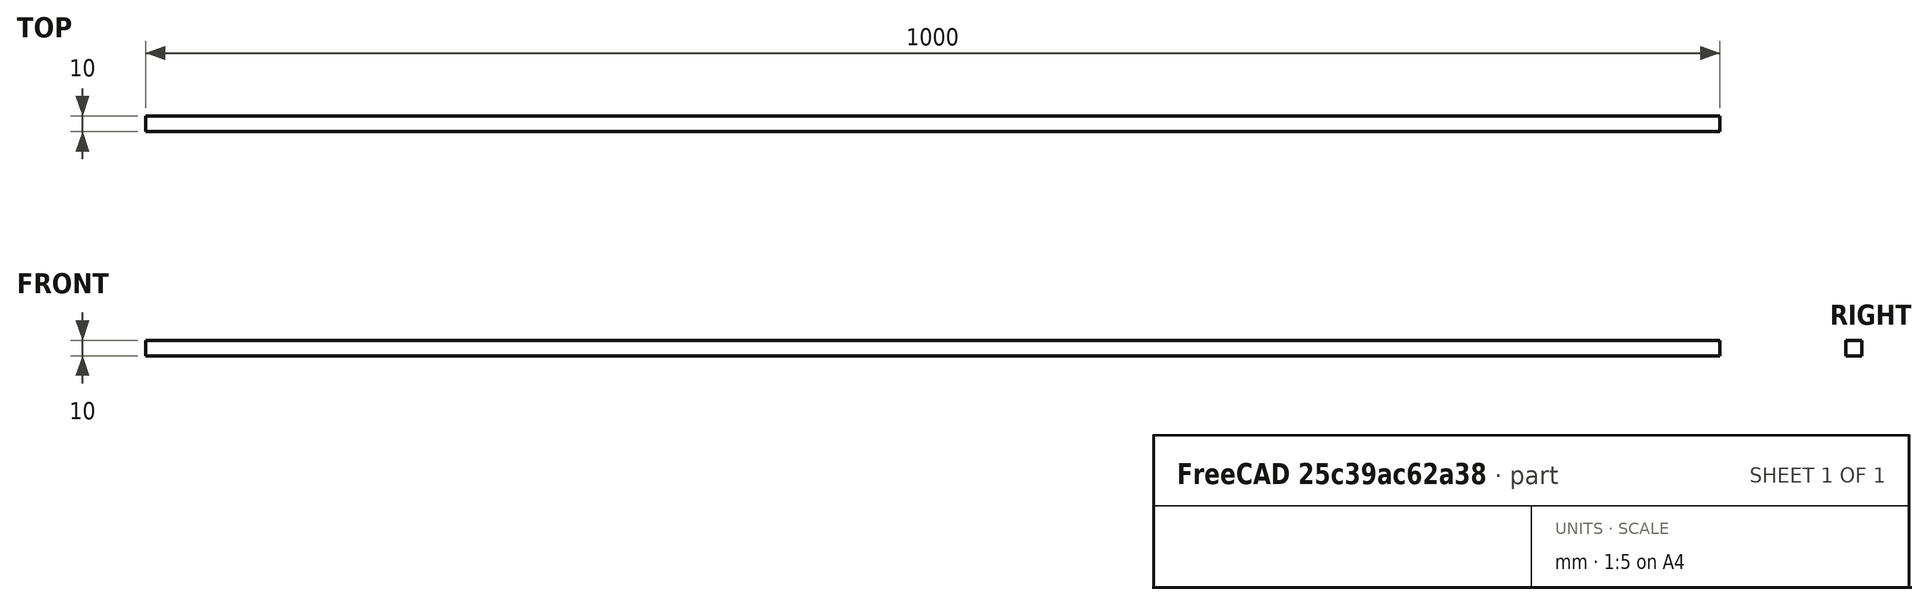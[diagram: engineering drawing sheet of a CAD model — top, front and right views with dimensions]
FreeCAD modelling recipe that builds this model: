
FCSTD DOCUMENT  (FreeCAD 0.21R33694 (Git))
Label: Bar buckling
License: All rights reserved
LicenseURL: http://en.wikipedia.org/wiki/All_rights_reserved
objects: Fem::FemMeshObjectPython×5, Fem::FemResultObjectPython×4, Part::Box×1, Fem::ConstraintFixed×1, Fem::ConstraintForce×1, App::MaterialObjectPython×1, Fem::FemSolverObjectPython×1, Fem::FemAnalysis×1
note: 1 computed .brp shape members not serialized (recipe doc carries the construction recipe); baked Part::Feature solids carry a one-line shape summary decoded from their .brp

FEATURE [Part::Box] Box  label="Cube"
  AttacherType = Attacher::AttachEngine3D
  Height = 10
  Length = 1000
  Width = 10
FEATURE [Fem::ConstraintFixed] ConstraintFixed
  NormalDirection = (-1,0,0)
  Normals = (9) [(-1,0,0),(-1,0,0),(-1,0,0),(-1,0,0),(-1,0,0),(-1,0,0),(-1,0,0),(-1,0,0),(-1,0,0)]
  Points = (9) [(0,10,0),(0,10,5),(0,10,10),(0,5,0),(0,5,5),(0,5,10),(0,0,0),(0,0,5),(0,0,10)]
  References = -> [Box]
FEATURE [Fem::ConstraintForce] ConstraintForce
  DirectionVector = (-1,0,0)
  Force = 1000
  NormalDirection = (1,0,0)
  Points = (9) [(1000,10,0),(1000,10,5),(1000,10,10),(1000,5,0),(1000,5,5),(1000,5,10),(1000,0,0),(1000,0,5),(1000,0,10)]
  References = -> [Box]
  Reversed = true
FEATURE [App::MaterialObjectPython] MaterialSolid  # material (typed FeaturePython)
  Category = 0
  Material = AuthorAndLicense=(c) 2014 M. Münch - GNU Lesser General Public License (LGPL),CardName=Steel-St-E-315,Density=7800 kg/m^3,Father=Metal,+13 more (map truncated)
FEATURE [Fem::FemMeshObjectPython] FEMMeshGmsh  # FEM object (typed FeaturePython)
  Algorithm2D = 0
  Algorithm3D = 0
  CharacteristicLengthMax = 50
  CharacteristicLengthMin = 0
  CoherenceMesh = true
  ElementDimension = 0
  ElementOrder = 1
  GeometryTolerance = 1e-06
  GroupsOfNodes = false
  HighOrderOptimize = 0
  MeshSizeFromCurvature = 12
  OptimizeNetgen = false
  OptimizeStd = true
  Part = -> Box
  RecombinationAlgorithm = 0
  Recombine3DAll = false
  RecombineAll = false
  SecondOrderLinear = false
FEATURE [Fem::FemSolverObjectPython] SolverCcxTools  # FEM object (typed FeaturePython)
  AnalysisType = 0
  BeamShellResultOutput3D = false
  BucklingFactors = 1
  EigenmodeHighLimit = 1000000
  EigenmodeLowLimit = 0
  EigenmodesCount = 10
  GeometricalNonlinearity = 0
  IterationsControlParameterCutb = 0.25,0.5,0.75,0.85,,,1.5,
  IterationsControlParameterIter = 4,8,9,200,10,400,,200,,
  IterationsControlParameterTimeUse = false
  IterationsThermoMechMaximum = 2000
  IterationsUserDefinedIncrementations = false
  IterationsUserDefinedTimeStepLength = false
  MaterialNonlinearity = 0
  MatrixSolverType = 0
  SplitInputWriter = false
  ThermoMechSteadyState = true
  TimeEnd = 1
  TimeInitialStep = 0.01
FEATURE [Fem::FemMeshObjectPython] Result_Mesh_Volume  # FEM object (typed FeaturePython)
FEATURE [Fem::FemResultObjectPython] ResultMechanical  label="ElasticPlasticDisplacementResults"  # FEM object (typed FeaturePython)
  CriticalStrainRatio = [0,0,0,0,0,0,0,0,0,0,0,0,0,0,0,0,0,0,0,0,0,0,0,0,0,0,0,0,0,0,0,0,0,0,0,0,0,0,0,0,0,0,0,0,0,0,0,0,0,0,0,0,0,0,0,0,0,0,0,0,0,0,0,0,0,0,0,0,0,0,0,0,0,0,0,0,0,0,0,0,0,0,0,0,0,0,0,0,0,0,0,0,0,0,0,0,0,0,0,0,0,0,0,0,0,0,0,0,0,0,0,0,0,0,0,0,0,0,0,0,+288 more]
  DisplacementLengths = [0,0,0,0,0.0477215,0.0477637,0.0476792,0.0477215,0,0,0,0,0.0477426,0.0477003,0.0477003,0.0477426,0.00230585,0.00470254,0.00709469,0.00948683,0.011879,0.0142713,0.0166636,0.0190559,0.0214482,0.0238405,0.0262328,0.0286251,0.0310174,0.0334098,+378 more]
  DisplacementVectors = (408) [(0,0,0),(0,0,0),(0,0,0),(0,0,0),(-0.0475136,-0.00321704,-0.00307423),(-0.0475465,-0.00321703,-0.00321709),(-0.0474806,-0.00307419,-0.00307422),+401 more]
  Eigenmode = 0
  EigenmodeFrequency = 0
  Mesh = -> Result_Mesh_Volume
  NodeNumbers = [1,2,3,4,5,6,7,8,9,10,11,12,13,14,15,16,17,18,19,20,21,22,23,24,25,26,27,28,29,30,31,32,33,34,35,36,37,38,39,40,41,42,43,44,45,46,47,48,49,50,51,52,53,54,55,56,57,58,59,60,61,62,63,64,65,66,67,68,69,+339 more]
  NodeStressXX = [0,0,0,0,0,0,0,0,0,0,0,0,0,0,0,0,0,0,0,0,0,0,0,0,0,0,0,0,0,0,0,0,0,0,0,0,0,0,0,0,0,0,0,0,0,0,0,0,0,0,0,0,0,0,0,0,0,0,0,0,0,0,0,0,0,0,0,0,0,0,0,0,0,0,0,0,0,0,0,0,0,0,0,0,0,0,0,0,0,0,0,0,0,0,0,0,0,0,0,0,0,0,0,0,0,0,0,0,0,0,0,0,0,0,0,0,0,0,0,0,+288 more]
  NodeStressXY = [0,0,0,0,0,0,0,0,0,0,0,0,0,0,0,0,0,0,0,0,0,0,0,0,0,0,0,0,0,0,0,0,0,0,0,0,0,0,0,0,0,0,0,0,0,0,0,0,0,0,0,0,0,0,0,0,0,0,0,0,0,0,0,0,0,0,0,0,0,0,0,0,0,0,0,0,0,0,0,0,0,0,0,0,0,0,0,0,0,0,0,0,0,0,0,0,0,0,0,0,0,0,0,0,0,0,0,0,0,0,0,0,0,0,0,0,0,0,0,0,+288 more]
  NodeStressXZ = [0,0,0,0,0,0,0,0,0,0,0,0,0,0,0,0,0,0,0,0,0,0,0,0,0,0,0,0,0,0,0,0,0,0,0,0,0,0,0,0,0,0,0,0,0,0,0,0,0,0,0,0,0,0,0,0,0,0,0,0,0,0,0,0,0,0,0,0,0,0,0,0,0,0,0,0,0,0,0,0,0,0,0,0,0,0,0,0,0,0,0,0,0,0,0,0,0,0,0,0,0,0,0,0,0,0,0,0,0,0,0,0,0,0,0,0,0,0,0,0,+288 more]
  NodeStressYY = [0,0,0,0,0,0,0,0,0,0,0,0,0,0,0,0,0,0,0,0,0,0,0,0,0,0,0,0,0,0,0,0,0,0,0,0,0,0,0,0,0,0,0,0,0,0,0,0,0,0,0,0,0,0,0,0,0,0,0,0,0,0,0,0,0,0,0,0,0,0,0,0,0,0,0,0,0,0,0,0,0,0,0,0,0,0,0,0,0,0,0,0,0,0,0,0,0,0,0,0,0,0,0,0,0,0,0,0,0,0,0,0,0,0,0,0,0,0,0,0,+288 more]
  NodeStressYZ = [0,0,0,0,0,0,0,0,0,0,0,0,0,0,0,0,0,0,0,0,0,0,0,0,0,0,0,0,0,0,0,0,0,0,0,0,0,0,0,0,0,0,0,0,0,0,0,0,0,0,0,0,0,0,0,0,0,0,0,0,0,0,0,0,0,0,0,0,0,0,0,0,0,0,0,0,0,0,0,0,0,0,0,0,0,0,0,0,0,0,0,0,0,0,0,0,0,0,0,0,0,0,0,0,0,0,0,0,0,0,0,0,0,0,0,0,0,0,0,0,+288 more]
  NodeStressZZ = [0,0,0,0,0,0,0,0,0,0,0,0,0,0,0,0,0,0,0,0,0,0,0,0,0,0,0,0,0,0,0,0,0,0,0,0,0,0,0,0,0,0,0,0,0,0,0,0,0,0,0,0,0,0,0,0,0,0,0,0,0,0,0,0,0,0,0,0,0,0,0,0,0,0,0,0,0,0,0,0,0,0,0,0,0,0,0,0,0,0,0,0,0,0,0,0,0,0,0,0,0,0,0,0,0,0,0,0,0,0,0,0,0,0,0,0,0,0,0,0,+288 more]
  Peeq = [0,0,0,0,0,0,0,0,0,0,0,0,0,0,0,0,0,0,0,0,0,0,0,0,0,0,0,0,0,0,0,0,0,0,0,0,0,0,0,0,0,0,0,0,0,0,0,0,0,0,0,0,0,0,0,0,0,0,0,0,0,0,0,0,0,0,0,0,0,0,0,0,0,0,0,0,0,0,0,0,0,0,0,0,0,0,0,0,0,0,0,0,0,0,0,0,0,0,0,0,0,0,0,0,0,0,0,0,0,0,0,0,0,0,0,0,0,0,0,0,+288 more]
  ResultType = Fem::ResultMechanical
  Stats = [-0.0475465,0,-0.00321704,8.59485e-05,-0.00321709,8.59484e-05,0,0.0477637,0,0,0,0,0,0,0,0,0,0,0,0,0,0,0,0,0,0]
  Temperature = [0,0,0,0,0,0,0,0,0,0,0,0,0,0,0,0,0,0,0,0,0,0,0,0,0,0,0,0,0,0,0,0,0,0,0,0,0,0,0,0,0,0,0,0,0,0,0,0,0,0,0,0,0,0,0,0,0,0,0,0,0,0,0,0,0,0,0,0,0,0,0,0,0,0,0,0,0,0,0,0,0,0,0,0,0,0,0,0,0,0,0,0,0,0,0,0,0,0,0,0,0,0,0,0,0,0,0,0,0,0,0,0,0,0,0,0,0,0,0,0,+288 more]
  Time = 0
  vonMises = [0,0,0,0,0,0,0,0,0,0,0,0,0,0,0,0,0,0,0,0,0,0,0,0,0,0,0,0,0,0,0,0,0,0,0,0,0,0,0,0,0,0,0,0,0,0,0,0,0,0,0,0,0,0,0,0,0,0,0,0,0,0,0,0,0,0,0,0,0,0,0,0,0,0,0,0,0,0,0,0,0,0,0,0,0,0,0,0,0,0,0,0,0,0,0,0,0,0,0,0,0,0,0,0,0,0,0,0,0,0,0,0,0,0,0,0,0,0,0,0,+288 more]
FEATURE [Fem::FemMeshObjectPython] Result_Mesh_Volume001  # FEM object (typed FeaturePython)
FEATURE [Fem::FemResultObjectPython] ResultMechanical001  label="ElasticDisplacementResults"  # FEM object (typed FeaturePython)
  DisplacementLengths = [0,0,0,0,0.0477215,0.0477637,0.0476792,0.0477215,0,0,0,0,0.0477426,0.0477003,0.0477003,0.0477426,0.00230585,0.00470254,0.00709469,0.00948683,0.011879,0.0142713,0.0166636,0.0190559,0.0214482,0.0238405,0.0262328,0.0286251,0.0310174,0.0334098,+378 more]
  DisplacementVectors = (408) [(0,0,0),(0,0,0),(0,0,0),(0,0,0),(-0.0475136,-0.00321704,-0.00307423),(-0.0475465,-0.00321703,-0.00321709),(-0.0474806,-0.00307419,-0.00307422),+401 more]
  Eigenmode = 0
  EigenmodeFrequency = 0
  Mesh = -> Result_Mesh_Volume001
  NodeNumbers = <same value as first occurrence — deduplicated (x4 in doc)>
  ResultType = Fem::ResultMechanical
  Stats = [-0.0475465,0,-0.00321704,8.59485e-05,-0.00321709,8.59484e-05,0,0.0477637,0,0,0,0,0,0,0,0,0,0,0,0,0,0,0,0,0,0]
  Time = 0
FEATURE [Fem::FemMeshObjectPython] Result_Mesh_Volume002  # FEM object (typed FeaturePython)
FEATURE [Fem::FemResultObjectPython] ResultMechanical002  label="ElasticBucklingShape_lambda1=0.435"  # FEM object (typed FeaturePython)
  DisplacementLengths = [1.95956e-07,6.56776e-08,5.82961e-08,1.93146e-07,1.17521,1.17515,1.17515,1.17521,1.15274e-07,1.24932e-07,1.02571e-07,1.37781e-07,1.17515,1.17517,1.17515,1.17517,0.0033802,0.0138478,0.0315134,0.0562738,0.0879756,0.126422,0.171374,0.222552,+384 more]
  DisplacementVectors = (408) [(-5.18528e-08,-1.09615e-07,1.5393e-07),(2.94457e-08,4.28781e-08,4.00995e-08),(-7.30465e-09,5.60633e-08,1.42122e-08),+405 more]
  Eigenmode = 0
  EigenmodeFrequency = 0
  Mesh = -> Result_Mesh_Volume002
  NodeNumbers = <same value as first occurrence — deduplicated (x4 in doc)>
  ResultType = Fem::ResultMechanical
  Stats = [-0.0127456,0.0127467,-0.617222,5.60633e-08,-8.0438e-08,1,1.33556e-08,1.17521,0,0,0,0,0,0,0,0,0,0,0,0,0,0,0,0,0,0]
  Time = 0
FEATURE [Fem::FemMeshObjectPython] Result_Mesh_Volume003  # FEM object (typed FeaturePython)
FEATURE [Fem::FemResultObjectPython] ResultMechanical003  label="ElasticBucklingShape_lambda2=0.435"  # FEM object (typed FeaturePython)
  DisplacementLengths = [5.20515e-08,2.77366e-07,2.12324e-07,6.16658e-08,1.17514,1.17521,1.17521,1.17514,1.31387e-07,1.02112e-07,1.24557e-07,1.07548e-07,1.17516,1.17515,1.17517,1.17515,0.00354108,0.0140088,0.0316737,0.0564323,0.0881308,0.126571,0.171518,0.222695,+384 more]
  DisplacementVectors = (408) [(-1.7967e-08,7.16444e-09,4.8324e-08),(-1.24409e-07,-1.74963e-07,-1.75621e-07),(3.08625e-08,-1.43506e-07,-1.53412e-07),+405 more]
  Eigenmode = 0
  EigenmodeFrequency = 0
  Mesh = -> Result_Mesh_Volume003
  NodeNumbers = <same value as first occurrence — deduplicated (x4 in doc)>
  ResultType = Fem::ResultMechanical
  Stats = [-0.0127489,0.0127437,-1,7.98686e-08,-0.617214,5.5543e-08,7.82558e-09,1.17521,0,0,0,0,0,0,0,0,0,0,0,0,0,0,0,0,0,0]
  Time = 0
FEATURE [Fem::FemAnalysis] Analysis
  Group = -> [ConstraintFixed,ConstraintForce,MaterialSolid,FEMMeshGmsh,SolverCcxTools,ResultMechanical,ResultMechanical001,ResultMechanical002,ResultMechanical003]
